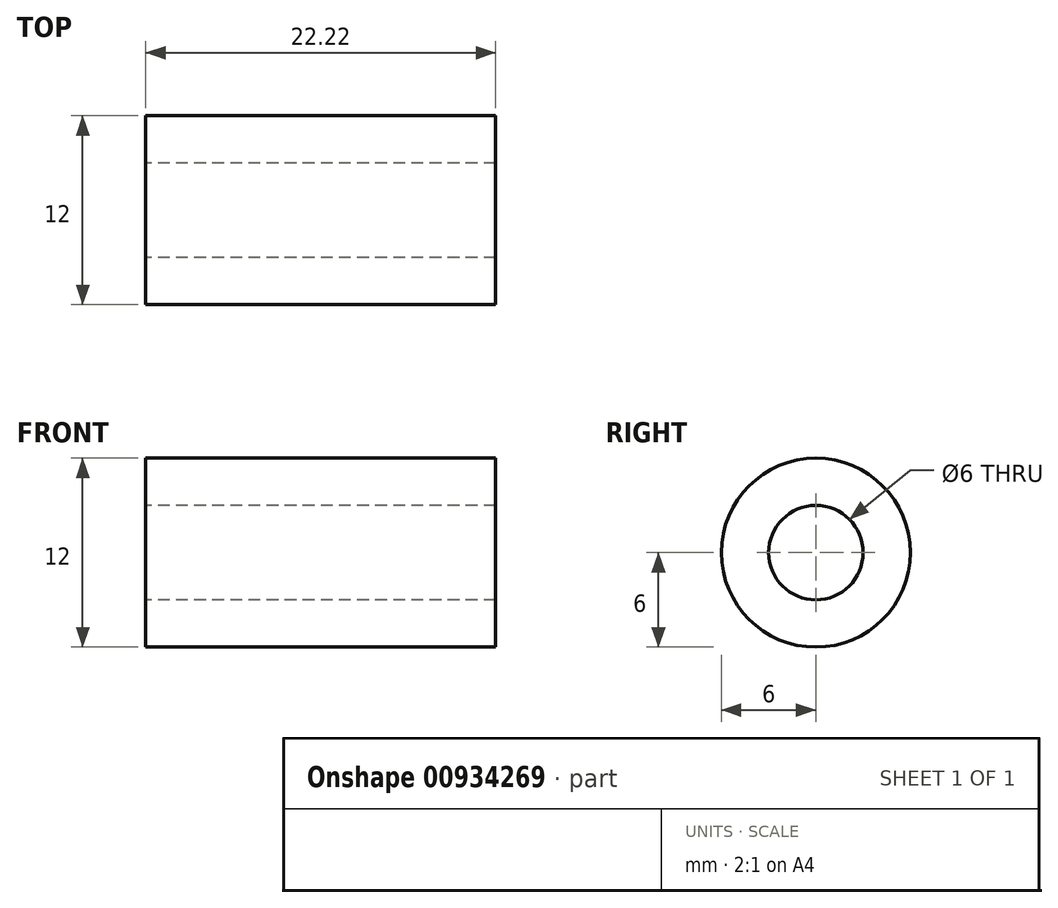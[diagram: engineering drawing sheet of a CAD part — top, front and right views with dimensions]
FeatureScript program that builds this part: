
annotation { "Feature Type Name" : "Feature", "Feature Type Description" : "" }
export const myFeature = defineFeature(function(context is Context, id is Id, definition is map)
    precondition{}
    {
        {
            var Q0;
            Q0=qCreatedBy(makeId("Right.planeOp"),FACE);
            var sketch = newSketch(context, id + "F0", { "sketchPlane" : qUnion([Q0])});
            skCircle(sketch, "E0", {"center": v(0, 0) * mm, "radius": 6 * mm});
            skCircle(sketch, "E1", {"center": v(0, 0) * mm, "radius": 3 * mm});
            skSolve(sketch);
        }
        {
            var Q0;
            Q0=makeQuery(id+"F0.imprint","IMPRINT",FACE,{"disambiguationData":[TD([[makeQuery(id+"F0.imprint","IMPRINT",EDGE,{"derivedFrom":sQuery(id+"F0.wireOp",EDGE,"E0")}),1.0]])]});
            extrude(context, id + "F1", {"entities" : qUnion([Q0]), "endBound" : BoundingType.SYMMETRIC, "depth" : 22.22 * mm, "offsetDistance" : 25 * mm});
        }
    });
